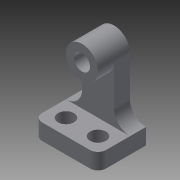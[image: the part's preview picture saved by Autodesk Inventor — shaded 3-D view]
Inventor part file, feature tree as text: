
AUTODESK INVENTOR PART (.ipt)
format: ipt  version: 2015 (Build 190159000, 159)  size: 132,608 bytes
history: native  units: in
note: dims shown in document units (in); Inventor stores cm internally (conversion verified against a paired STEP export)
features: sketch x4, extrude x3, fillet x2, hole x2
ambient origin geometry x8: Origin, YZ Plane, XZ Plane, XY Plane, X Axis, Y Axis, Z Axis, Center Point
bodies: Solid1 (feature_tree)
feature tree (11):
  sketch  "Sketch1"  dims[d0=2.0in d1=0.5in d2=0.5in]
  extrude  "Extrusion1"  Depth=0.5in
  fillet  "Fillet1"  Radius=0.5in
  extrude  "Extrusion2"  Depth=0.5in
  sketch  "Sketch3"  dims[d6=1.75in d7=1.5in d8=0.0in]
  extrude  "Extrusion3"  Depth=1.5in TaperAngle=0.0deg
  hole  "Hole1"  [1 undecoded]
  hole  "Hole2"  [1 undecoded]
  fillet  "Fillet2"  Radius=0.5in
  sketch  "Sketch2"  dims[d3=0.5in d5=0.5in]
  sketch  "Sketch4"  dims[d9=0.25in d10=1.0in d11=0.0in d12=0.5in d13=0.0in d14=0.5in d15=0.75in d16=0.375in d17=0.25in d18=0.5635in d19=1.0in d20=0.8108in d21=0.5in d22=0.5in d23=0.5in d24=0.5in d25=0.5in d26=0.75in d27=0.375in d28=0.25in d29=0.5635in d30=1.0in d31=0.8108in d32=0.5in]
note: 2 required parameter values undecoded (feature->parameter linkage not recoverable at this tier; creation-order binding heuristic only, values carry confidence <= 0.55)
